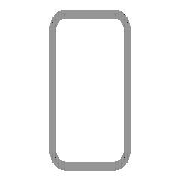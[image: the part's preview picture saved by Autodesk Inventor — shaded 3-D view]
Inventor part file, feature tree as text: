
AUTODESK INVENTOR PART (.ipt)
format: ipt  version: 2025 (Build 290162010, 162A)  size: 133,632 bytes
history: native  units: mm (DEFAULTED — no unit token found)
features: other x4, sketch x1, plane x1
ambient origin geometry x8: Origin, YZ Plane, XZ Plane, XY Plane, X Axis, Y Axis, Z Axis, Center Point
bodies: Solid1 (feature_tree), Body (feature_tree)
feature tree (6):
  parser-record x1  (decoder bookkeeping rows leaked as tree rows — omitted from the tree; the rows remain in map.json)
  other  "Driven Length"
  other  "Start Plane"
  other  "End Plane"
  sketch  "Sketch3"  dims[d3=2200.0mm d4=0.0mm d7=4.0mm d9=40.0mm d11=80.0mm d12=2.0mm d13=-0.0mm d14=2200.0mm d15=20.0mm d16=40.0mm d17=90.0deg d18=2200.0mm]
  plane  "Work Plane3"
